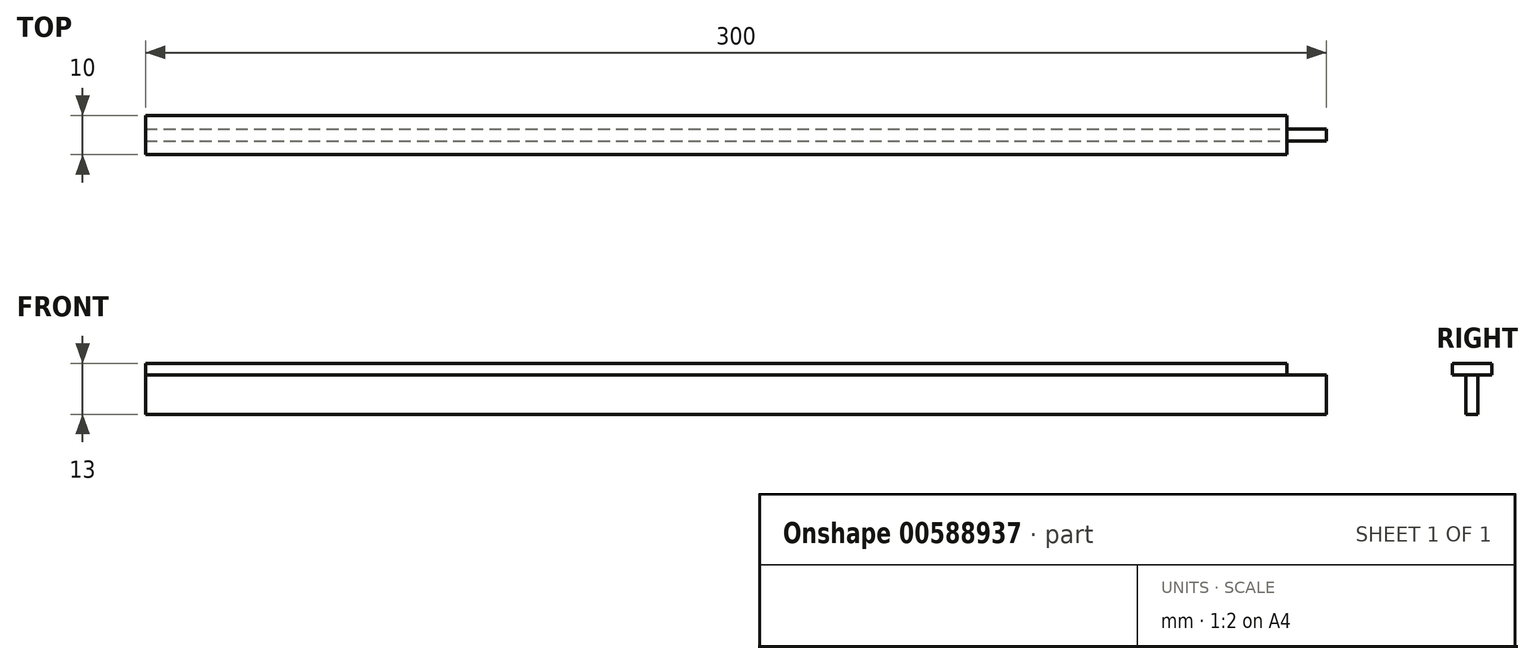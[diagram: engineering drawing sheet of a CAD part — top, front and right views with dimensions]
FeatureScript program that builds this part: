
annotation { "Feature Type Name" : "Feature", "Feature Type Description" : "" }
export const myFeature = defineFeature(function(context is Context, id is Id, definition is map)
    precondition{}
    {
        {
            var Q0;
            Q0=qCreatedBy(makeId("Front.planeOp"),FACE);
            var sketch = newSketch(context, id + "F0", { "sketchPlane" : qUnion([Q0])});
            skLineSegment(sketch, "E0.bottom", {"start": v(-126.93, -18.62) * mm, "end": v(163.07, -18.62) * mm});
            skLineSegment(sketch, "E0.top", {"start": v(-126.93, -21.62) * mm, "end": v(163.07, -21.62) * mm});
            skLineSegment(sketch, "E0.left", {"start": v(-126.93, -18.62) * mm, "end": v(-126.93, -21.62) * mm});
            skLineSegment(sketch, "E0.right", {"start": v(163.07, -18.62) * mm, "end": v(163.07, -21.62) * mm});
            skSolve(sketch);
        }
        {
            var Q0;
            Q0 = qSketchRegion(id + "F0", true);
            extrude(context, id + "F1", {"entities" : qUnion([Q0]), "endBound" : BoundingType.SYMMETRIC, "depth" : 10 * mm, "offsetDistance" : 25 * mm});
        }
        {
            var Q0;
            Q0=qCreatedBy(makeId("Front.planeOp"),FACE);
            var sketch = newSketch(context, id + "F2", { "sketchPlane" : qUnion([Q0])});
            skLineSegment(sketch, "E1.bottom", {"start": v(-126.93, -21.62) * mm, "end": v(173.07, -21.62) * mm});
            skLineSegment(sketch, "E1.top", {"start": v(-126.93, -31.62) * mm, "end": v(173.07, -31.62) * mm});
            skLineSegment(sketch, "E1.left", {"start": v(-126.93, -21.62) * mm, "end": v(-126.93, -31.62) * mm});
            skLineSegment(sketch, "E1.right", {"start": v(173.07, -21.62) * mm, "end": v(173.07, -31.62) * mm});
            skSolve(sketch);
        }
        {
            var Q0;
            Q0=makeQuery(id+"F2.imprint","IMPRINT",FACE,{"disambiguationData":[TD([[makeQuery(id+"F2.imprint","IMPRINT",EDGE,{"derivedFrom":sQuery(id+"F2.wireOp",EDGE,"E1.bottom")}),-1.0]])]});
            extrude(context, id + "F3", {"entities" : qUnion([Q0]), "operationType" : NewBodyOperationType.ADD, "endBound" : BoundingType.SYMMETRIC, "depth" : 3 * mm, "offsetDistance" : 25 * mm});
        }
    });
